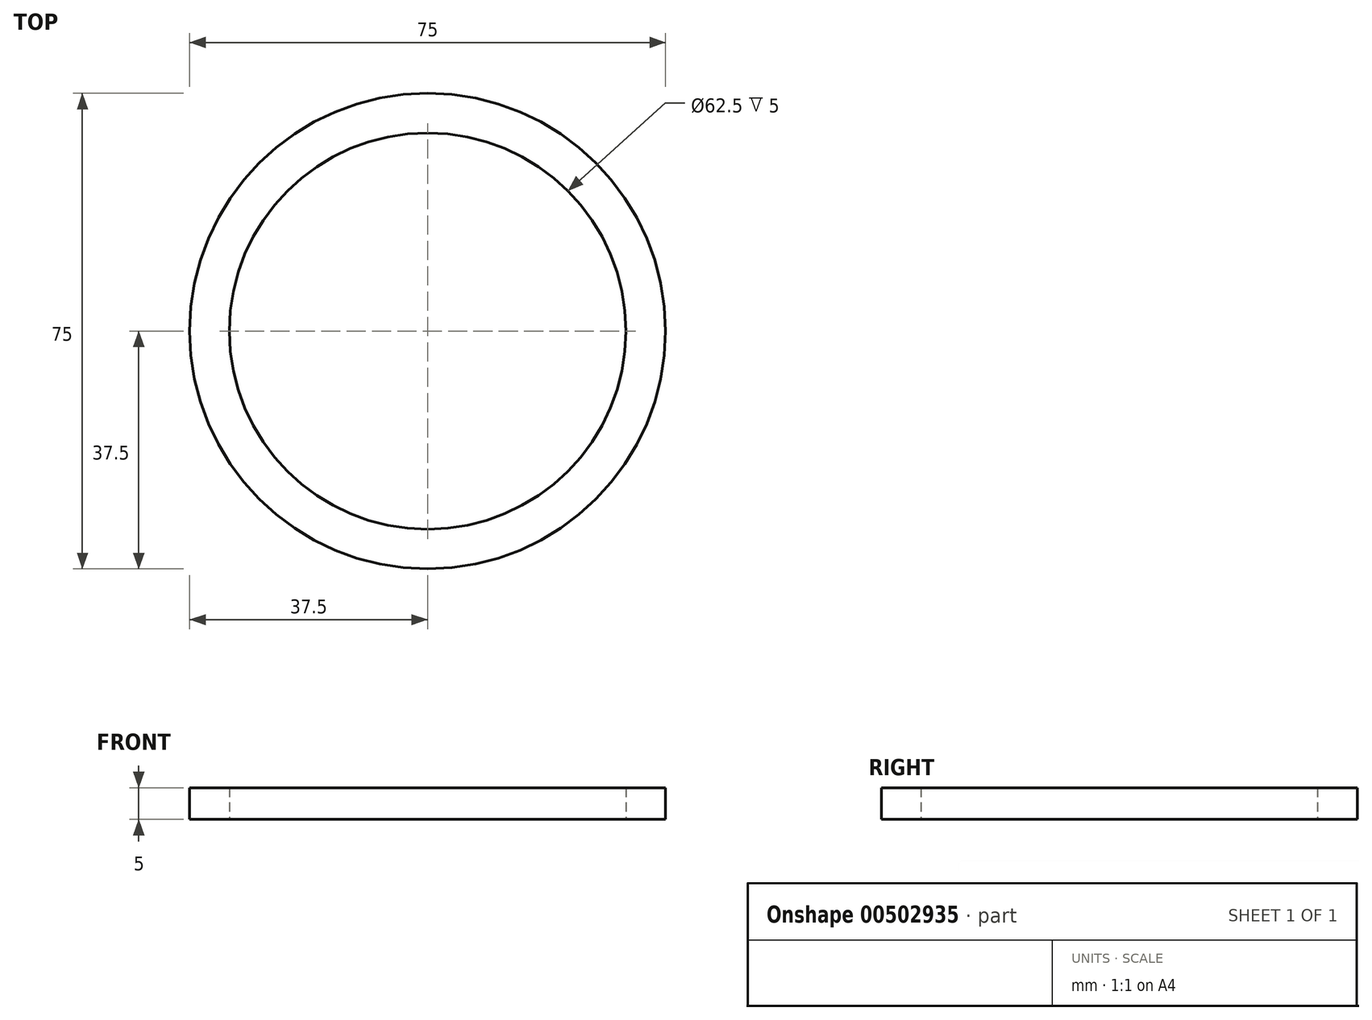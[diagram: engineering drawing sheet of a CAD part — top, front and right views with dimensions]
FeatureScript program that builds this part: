
annotation { "Feature Type Name" : "Feature", "Feature Type Description" : "" }
export const myFeature = defineFeature(function(context is Context, id is Id, definition is map)
    precondition{}
    {
        {
            assignVariable(context, id + "F0", {"name" : "height", "anyValue" : 5});
        }
        {
            var Q0;
            Q0=qCreatedBy(makeId("Top.planeOp"),FACE);
            var sketch = newSketch(context, id + "F1", { "sketchPlane" : qUnion([Q0])});
            skCircle(sketch, "E0", {"center": v(0, 0) * mm, "radius": 37.5 * mm});
            skCircle(sketch, "E1", {"center": v(0, 0) * mm, "radius": 31.25 * mm});
            skSolve(sketch);
        }
        {
            var Q0;
            Q0=makeQuery(id+"F1.imprint","IMPRINT",FACE,{"disambiguationData":[TD([[makeQuery(id+"F1.imprint","IMPRINT",EDGE,{"derivedFrom":sQuery(id+"F1.wireOp",EDGE,"E0")}),1.0]])]});
            var Q1;
            Q1=sQuery(id+"F1.wireOp",EDGE,"E0");
            extrude(context, id + "F2", {"entities" : qUnion([Q0]), "surfaceEntities" : qUnion([Q1]), "depth" : (getVariable(context, 'height')) * mm});
        }
    });
